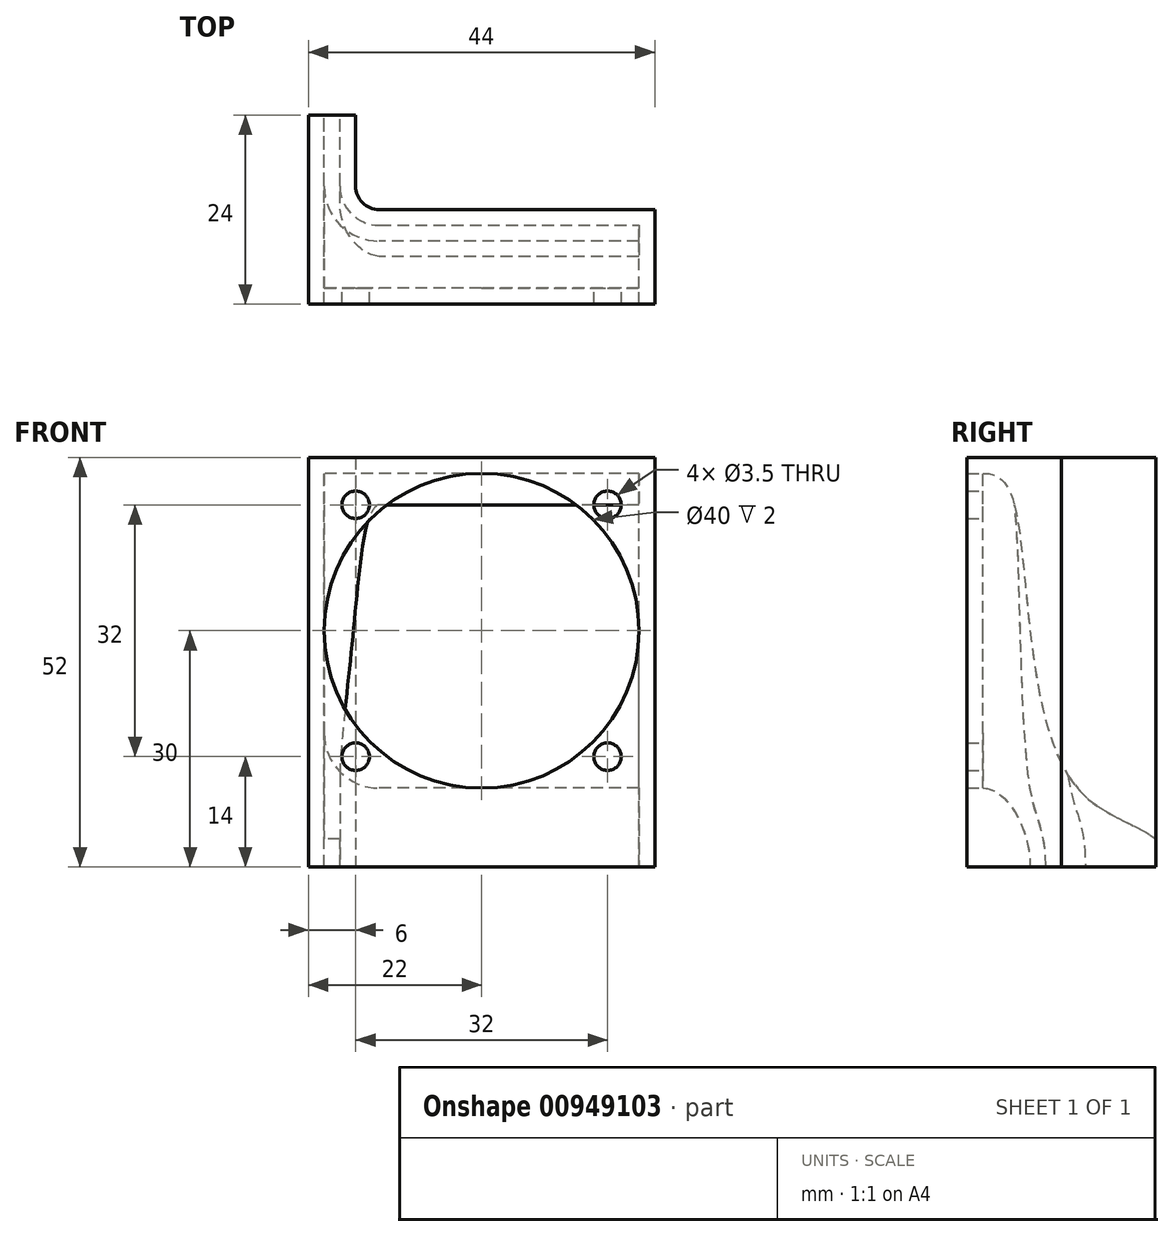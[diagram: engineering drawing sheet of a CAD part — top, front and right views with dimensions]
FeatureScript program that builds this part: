
annotation { "Feature Type Name" : "Feature", "Feature Type Description" : "" }
export const myFeature = defineFeature(function(context is Context, id is Id, definition is map)
    precondition{}
    {
        {
            var Q0;
            Q0=qCreatedBy(makeId("Right.planeOp"),FACE);
            var sketch = newSketch(context, id + "F0", { "sketchPlane" : qUnion([Q0])});
            skLineSegment(sketch, "E0", {"start": v(0, 0) * mm, "end": v(0, 40) * mm});
            skFitSpline(sketch, "E1", {"points": [v(0, 40) * mm, v(4, 36) * mm, v(12, 0) * mm, v(24, -10) * mm], "startDerivative": vector(31.3, 0) * mm, "endDerivative": vector(0, -47.07) * mm});
            skFitSpline(sketch, "E2", {"points": [v(0, 0) * mm, v(6, -10) * mm], "startDerivative": vector(9, 0) * mm, "endDerivative": vector(0, -15) * mm});
            skLineSegment(sketch, "E3", {"start": v(6, -10) * mm, "end": v(24, -10) * mm});
            skFitSpline(sketch, "E4", {"points": [v(8, -10) * mm, v(6, 0) * mm, v(4, 36) * mm], "startDerivative": vector(0, 43.2) * mm, "endDerivative": vector(-3.86, 22.65) * mm});
            skSolve(sketch);
        }
        {
            var Q0;
            {var subQ3=sQuery(id+"F0.wireOp",EDGE,"E4");Q0=makeQuery(id+"F0.imprint","IMPRINT",FACE,{"disambiguationData":[TD([[makeQuery(id+"F0.imprint","IMPRINT",EDGE,{"derivedFrom":subQ3}),-1.0]])]});}
            var Q1;
            {var subQ4=sQuery(id+"F0.wireOp",EDGE,"E0");Q1=makeQuery(id+"F0.imprint","IMPRINT",FACE,{"disambiguationData":[TD([[makeQuery(id+"F0.imprint","IMPRINT",EDGE,{"derivedFrom":subQ4}),-1.0]])]});}
            extrude(context, id + "F1", {"entities" : qUnion([Q0, Q1]), "endBound" : BoundingType.SYMMETRIC, "depth" : 40 * mm, "offsetDistance" : 25 * mm});
        }
        {
            var Q0;
            {var subQ3=sQuery(id+"F0.wireOp",EDGE,"E4");Q0=makeQuery(id+"F0.imprint","IMPRINT",FACE,{"disambiguationData":[TD([[makeQuery(id+"F0.imprint","IMPRINT",EDGE,{"derivedFrom":subQ3}),-1.0]])]});}
            extrude(context, id + "F2", {"entities" : qUnion([Q0]), "operationType" : NewBodyOperationType.REMOVE, "oppositeDirection" : true, "depth" : 18 * mm, "offsetDistance" : 25 * mm, "hasSecondDirection" : true, "secondDirectionOppositeDirection" : false, "secondDirectionDepth" : 20 * mm});
        }
        {
            var Q0;
            Q0=qCreatedBy(makeId("Front.planeOp"),FACE);
            var sketch = newSketch(context, id + "F3", { "sketchPlane" : qUnion([Q0])});
            skLineSegment(sketch, "E5.0", {"start": v(20, 40) * mm, "end": v(-20, 40) * mm, "construction": true});
            skLineSegment(sketch, "E5.1", {"start": v(20, 0) * mm, "end": v(20, 40) * mm, "construction": true});
            skLineSegment(sketch, "E5.2", {"start": v(20, 0) * mm, "end": v(-20, 0) * mm, "construction": true});
            skLineSegment(sketch, "E5.3", {"start": v(-20, 0) * mm, "end": v(-20, 40) * mm, "construction": true});
            skCircle(sketch, "E6", {"center": v(0, 20) * mm, "radius": 20 * mm});
            skPoint(sketch, "E6.centerSnap0", {"position": v(-20, 20) * mm});
            skCircle(sketch, "E7", {"center": v(-16, 36) * mm, "radius": 1.75 * mm});
            skCircle(sketch, "E8", {"center": v(16, 36) * mm, "radius": 1.75 * mm});
            skCircle(sketch, "E9", {"center": v(-16, 4) * mm, "radius": 1.75 * mm});
            skCircle(sketch, "E10", {"center": v(16, 4) * mm, "radius": 1.75 * mm});
            skSolve(sketch);
        }
        {
            var Q0;
            Q0=makeQuery(id+"F3.imprint","IMPRINT",FACE,{"disambiguationData":[TD([[makeQuery(id+"F3.imprint","IMPRINT",EDGE,{"derivedFrom":sQuery(id+"F3.wireOp",EDGE,"E7")}),1.0]])]});
            var Q1;
            Q1=makeQuery(id+"F3.imprint","IMPRINT",FACE,{"disambiguationData":[TD([[makeQuery(id+"F3.imprint","IMPRINT",EDGE,{"derivedFrom":sQuery(id+"F3.wireOp",EDGE,"E6")}),1.0]])]});
            var Q2;
            Q2=makeQuery(id+"F3.imprint","IMPRINT",FACE,{"disambiguationData":[TD([[makeQuery(id+"F3.imprint","IMPRINT",EDGE,{"derivedFrom":sQuery(id+"F3.wireOp",EDGE,"E8")}),1.0]])]});
            var Q3;
            Q3=makeQuery(id+"F3.imprint","IMPRINT",FACE,{"disambiguationData":[TD([[makeQuery(id+"F3.imprint","IMPRINT",EDGE,{"derivedFrom":sQuery(id+"F3.wireOp",EDGE,"E10")}),1.0]])]});
            var Q4;
            Q4=makeQuery(id+"F3.imprint","IMPRINT",FACE,{"disambiguationData":[TD([[makeQuery(id+"F3.imprint","IMPRINT",EDGE,{"derivedFrom":sQuery(id+"F3.wireOp",EDGE,"E9")}),1.0]])]});
            extrude(context, id + "F4", {"entities" : qUnion([Q0, Q1, Q2, Q3, Q4]), "operationType" : NewBodyOperationType.ADD, "depth" : 2 * mm, "offsetDistance" : 25 * mm});
        }
        {
            var Q0;
            Q0=makeQuery(id+"F9.opBoolean","COPY",EDGE,{"derivedFrom":makeQuery(id+"F2.boolean.opBoolean","COPY",EDGE,{"derivedFrom":makeQuery(id+"F2.opExtrude","CAP_EDGE",EDGE,{"disambiguationData":[OSD([sQuery(id+"F0.wireOp",EDGE,"E4")])],"isStart":false})})});
            var Q1;
            Q1=makeQuery(id+"F2.boolean.opBoolean","COPY",EDGE,{"derivedFrom":makeQuery(id+"F2.opExtrude","CAP_EDGE",EDGE,{"disambiguationData":[OSD([sQuery(id+"F0.wireOp",EDGE,"E4")])],"isStart":false})});
            fillet(context, id + "F5", {"entities" : qUnion([Q0, Q1]), "radius" : 5 * mm, "tangentPropagation" : true, "allowEdgeOverflow" : false});
        }
        {
            var Q0;
            Q0=makeQuery(id+"F8.opExtrude","CAP_EDGE",EDGE,{"disambiguationData":[OSD([sQuery(id+"F7.wireOp",EDGE,"E13")])],"isStart":true});
            var Q1;
            Q1=makeQuery(id+"F1.opExtrude","CAP_EDGE",EDGE,{"disambiguationData":[OSD([sQuery(id+"F0.wireOp",EDGE,"E2")])],"isStart":true});
            fillet(context, id + "F6", {"entities" : qUnion([Q0, Q1]), "radius" : 7 * mm, "tangentPropagation" : true, "allowEdgeOverflow" : false});
        }
        {
            var Q0;
            Q0=makeQuery(id+"F4.opExtrude","CAP_FACE",FACE,{"disambiguationData":[OSD([sQuery(id+"F3.wireOp",EDGE,"E6")])],"isStart":false});
            var sketch = newSketch(context, id + "F7", { "sketchPlane" : qUnion([Q0])});
            skLineSegment(sketch, "E11.0", {"start": v(20, 40) * mm, "end": v(0, 40) * mm});
            skLineSegment(sketch, "E11.1", {"start": v(0, 40) * mm, "end": v(-20, 40) * mm});
            skLineSegment(sketch, "E11.2", {"start": v(20, 20) * mm, "end": v(20, 40) * mm});
            skLineSegment(sketch, "E11.3", {"start": v(20, 0) * mm, "end": v(20, 20) * mm});
            skFitSpline(sketch, "E11.4", {"points": [v(20, 0) * mm, v(20, -3.33) * mm, v(20, -6.67) * mm, v(20, -10) * mm]});
            skLineSegment(sketch, "E11.5", {"start": v(20, -10) * mm, "end": v(-20, -10) * mm});
            skFitSpline(sketch, "E11.6", {"points": [v(-20, 0) * mm, v(-20, -3.33) * mm, v(-20, -6.67) * mm, v(-20, -10) * mm]});
            skLineSegment(sketch, "E11.7", {"start": v(-20, 0) * mm, "end": v(-20, 20) * mm});
            skLineSegment(sketch, "E11.8", {"start": v(-20, 20) * mm, "end": v(-20, 40) * mm});
            skLineSegment(sketch, "E12", {"start": v(-20, -10) * mm, "end": v(-22, -10) * mm});
            skLineSegment(sketch, "E13", {"start": v(-22, -10) * mm, "end": v(-22, 42) * mm});
            skLineSegment(sketch, "E14", {"start": v(-22, 42) * mm, "end": v(22, 42) * mm});
            skLineSegment(sketch, "E15", {"start": v(22, 42) * mm, "end": v(22, -10) * mm});
            skLineSegment(sketch, "E16", {"start": v(22, -10) * mm, "end": v(20, -10) * mm});
            skSolve(sketch);
        }
        {
            var Q0;
            Q0 = qSketchRegion(id + "F7", true);
            extrude(context, id + "F8", {"entities" : qUnion([Q0]), "oppositeDirection" : true, "depth" : 24 * mm, "offsetDistance" : 25 * mm});
        }
        {
            var Q0;
            Q0=makeQuery(id+"F1.opExtrude","SWEPT_BODY",BODY,{"disambiguationData":[OSD([sQuery(id+"F0.wireOp",EDGE,"E0"),sQuery(id+"F0.wireOp",EDGE,"E1"),sQuery(id+"F0.wireOp",EDGE,"E2"),sQuery(id+"F0.wireOp",EDGE,"E3")])]});
            var Q1;
            Q1=makeQuery(id+"F8.opExtrude","SWEPT_BODY",BODY,{"disambiguationData":[OSD([sQuery(id+"F7.wireOp",EDGE,"E11.5"),sQuery(id+"F7.wireOp",EDGE,"E12"),sQuery(id+"F7.wireOp",EDGE,"E13"),sQuery(id+"F7.wireOp",EDGE,"E14"),sQuery(id+"F7.wireOp",EDGE,"E15"),sQuery(id+"F7.wireOp",EDGE,"E16")])]});
            booleanBodies(context, id + "F9", {"operationType" : BooleanOperationType.SUBTRACTION, "tools" : qUnion([Q0]), "targets" : qUnion([Q1])});
        }
        {
            var Q0;
            Q0=makeQuery(id+"F8.opExtrude","SWEPT_FACE",FACE,{"disambiguationData":[OSD([sQuery(id+"F7.wireOp",EDGE,"E11.5"),sQuery(id+"F7.wireOp",EDGE,"E12"),sQuery(id+"F7.wireOp",EDGE,"E16")])]});
            var sketch = newSketch(context, id + "F10", { "sketchPlane" : qUnion([Q0])});
            skLineSegment(sketch, "E17.0", {"start": v(-18, -8) * mm, "end": v(20, -8) * mm, "construction": true});
            skLineSegment(sketch, "E17.6", {"start": v(-18, -8) * mm, "end": v(-18, -16) * mm, "construction": true});
            skLineSegment(sketch, "E17.8", {"start": v(22, 2) * mm, "end": v(-22, 2) * mm});
            skLineSegment(sketch, "E17.9", {"start": v(-22, -22) * mm, "end": v(-22, 2) * mm});
            skLineSegment(sketch, "E17.10", {"start": v(-20, -22) * mm, "end": v(-22, -22) * mm});
            skLineSegment(sketch, "E18", {"start": v(22, -10) * mm, "end": v(-13, -10) * mm});
            skLineSegment(sketch, "E19", {"start": v(-16, -13) * mm, "end": v(-16, -22) * mm});
            skPoint(sketch, "E20.visualSharp", {"position": v(-16, -10) * mm});
            skArc(sketch, "E20.filletArc", {"start": v(-13, -10) * mm, "mid": v(-15.12, -10.88) * mm, "end": v(-16, -13) * mm});
            skSolve(sketch);
        }
        {
            var Q0;
            {var subQ0=sQuery(id+"F10.wireOp",EDGE,"uXui7Q4t-d0mB-ENsy-KZza-r1dgIroBUFKR");Q0=makeQuery(id+"F10.imprint","IMPRINT",FACE,{"disambiguationData":[TD([[makeQuery(id+"F10.imprint","IMPRINT",EDGE,{"derivedFrom":subQ0}),1.0]])]});}
            var Q1;
            {var subQ4=sQuery(id+"F10.wireOp",EDGE,"E18");Q1=makeQuery(id+"F10.imprint","IMPRINT",FACE,{"disambiguationData":[TD([[makeQuery(id+"F10.imprint","IMPRINT",EDGE,{"derivedFrom":subQ4}),1.0]])]});}
            extrude(context, id + "F11", {"entities" : qUnion([Q0, Q1]), "operationType" : NewBodyOperationType.REMOVE, "endBound" : BoundingType.THROUGH_ALL, "oppositeDirection" : true, "depth" : 50 * mm, "offsetDistance" : 25 * mm});
        }
    });
